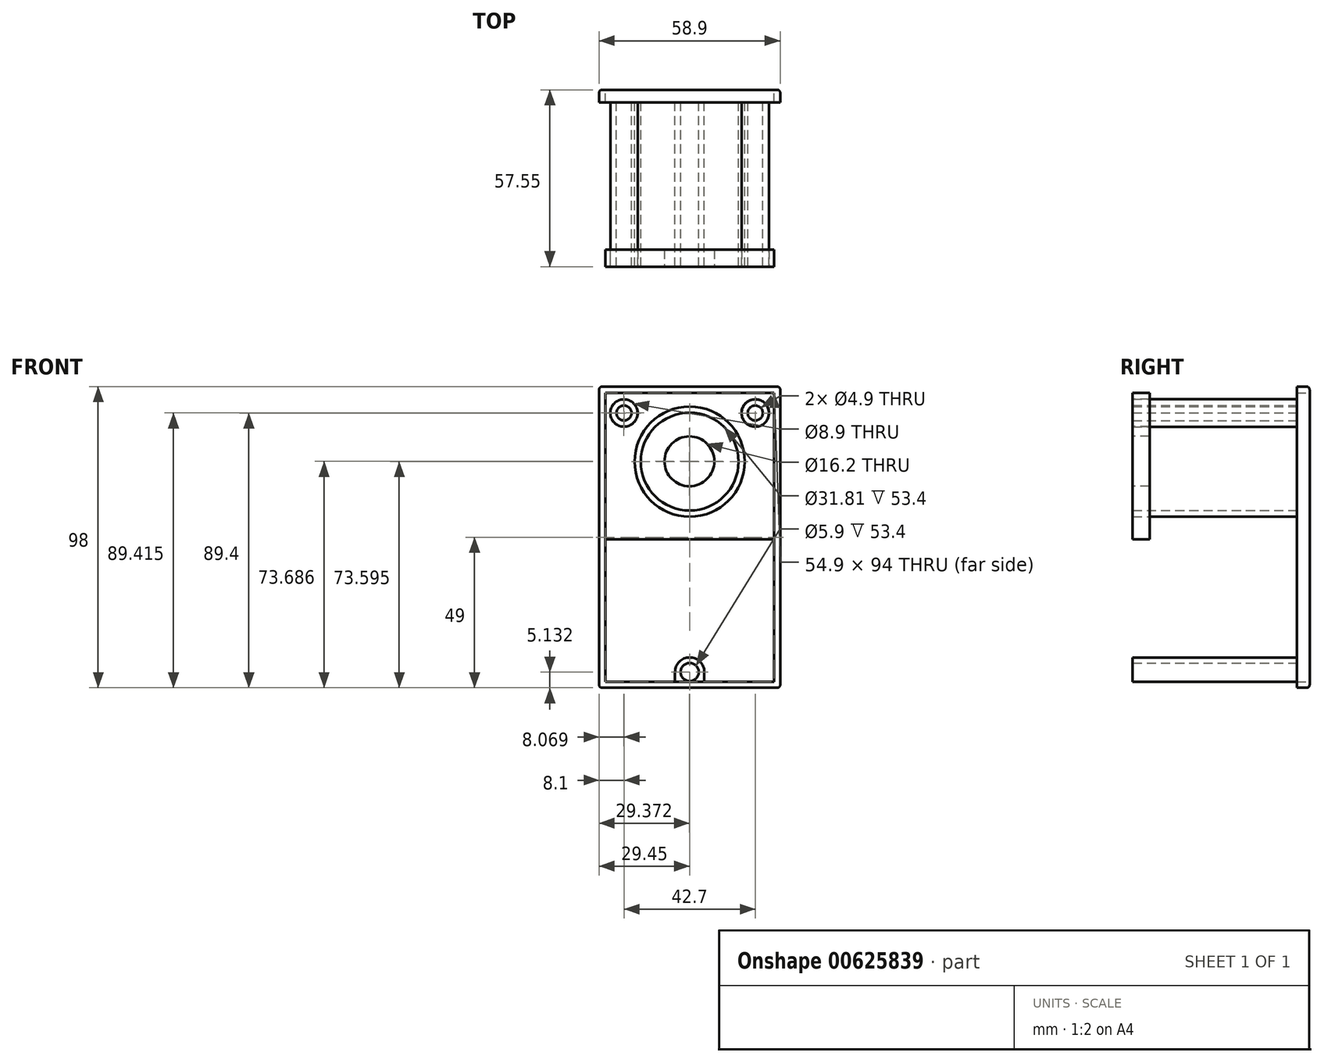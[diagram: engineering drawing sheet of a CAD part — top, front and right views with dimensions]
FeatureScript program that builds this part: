
annotation { "Feature Type Name" : "Feature", "Feature Type Description" : "" }
export const myFeature = defineFeature(function(context is Context, id is Id, definition is map)
    precondition{}
    {
        {
            var Q0;
            Q0=qCreatedBy(makeId("Front.planeOp"),FACE);
            var sketch = newSketch(context, id + "F0", { "sketchPlane" : qUnion([Q0])});
            skLineSegment(sketch, "E0.bottom", {"start": v(29.45, -49) * mm, "end": v(-29.45, -49) * mm});
            skLineSegment(sketch, "E0.top", {"start": v(29.45, 49) * mm, "end": v(-29.45, 49) * mm});
            skLineSegment(sketch, "E0.left", {"start": v(29.45, -49) * mm, "end": v(29.45, 49) * mm});
            skLineSegment(sketch, "E0.right", {"start": v(-29.45, -49) * mm, "end": v(-29.45, 49) * mm});
            skPoint(sketch, "E0.middle", {"position": v(0, 0) * mm});
            skCircle(sketch, "E1", {"center": v(0, 24.6) * mm, "radius": 15.9 * mm});
            skCircle(sketch, "E2", {"center": v(-21.35, 40.4) * mm, "radius": 4.4 * mm});
            skCircle(sketch, "E3", {"center": v(21.35, 40.4) * mm, "radius": 4.4 * mm});
            skCircle(sketch, "E4", {"center": v(-21.35, 40.4) * mm, "radius": 2.45 * mm});
            skCircle(sketch, "E5", {"center": v(21.35, 40.4) * mm, "radius": 2.45 * mm});
            skSolve(sketch);
        }
        {
            var Q0;
            Q0=makeQuery(id+"F0.imprint","IMPRINT",FACE,{"disambiguationData":[TD([[makeQuery(id+"F0.imprint","IMPRINT",EDGE,{"derivedFrom":sQuery(id+"F0.wireOp",EDGE,"E0.bottom")}),-1.0]])]});
            var Q1;
            Q1=makeQuery(id+"F0.imprint","IMPRINT",FACE,{"disambiguationData":[TD([[makeQuery(id+"F0.imprint","IMPRINT",EDGE,{"derivedFrom":sQuery(id+"F0.wireOp",EDGE,"E2")}),1.0]])]});
            var Q2;
            Q2=makeQuery(id+"F0.imprint","IMPRINT",FACE,{"disambiguationData":[TD([[makeQuery(id+"F0.imprint","IMPRINT",EDGE,{"derivedFrom":sQuery(id+"F0.wireOp",EDGE,"E3")}),1.0]])]});
            extrude(context, id + "F1", {"entities" : qUnion([Q0, Q1, Q2]), "depth" : 57.55 * mm, "offsetDistance" : 25 * mm});
        }
        {
            var Q0;
            Q0=makeQuery(id+"F1.opExtrude","CAP_FACE",FACE,{"disambiguationData":[OSD([sQuery(id+"F0.wireOp",EDGE,"E0.bottom"),sQuery(id+"F0.wireOp",EDGE,"E0.top"),sQuery(id+"F0.wireOp",EDGE,"E0.left"),sQuery(id+"F0.wireOp",EDGE,"E0.right"),sQuery(id+"F0.wireOp",EDGE,"E1"),sQuery(id+"F0.wireOp",EDGE,"E2"),sQuery(id+"F0.wireOp",EDGE,"E3")])],"isStart":false});
            shell(context, id + "F2", {"entities" : qUnion([Q0]), "thickness" : 2 * mm});
        }
        {
            var Q0;
            {var subQ0=sQuery(id+"F0.wireOp",EDGE,"E5");var subQ1=sQuery(id+"F0.wireOp",EDGE,"E4");var subQ2=sQuery(id+"F0.wireOp",EDGE,"E1");var subQ3=sQuery(id+"F0.wireOp",EDGE,"E0.right");var subQ4=sQuery(id+"F0.wireOp",EDGE,"E0.left");var subQ5=sQuery(id+"F0.wireOp",EDGE,"E0.top");var subQ6=sQuery(id+"F0.wireOp",EDGE,"E0.bottom");Q0=makeQuery(id+"F2.opShell","OFFSET_FACE",FACE,{"disambiguationData":[OSD([subQ6,subQ5,subQ4,subQ3,subQ2,subQ1,subQ0]),TDD([makeQuery(id+"F1.opExtrude","CAP_FACE",FACE,{"disambiguationData":[OSD([subQ6,subQ5,subQ4,subQ3,subQ2,subQ1,subQ0])],"isStart":false})]),OD(0.0)]});}
            extrude(context, id + "F3", {"entities" : qUnion([Q0]), "operationType" : NewBodyOperationType.REMOVE, "oppositeDirection" : true, "depth" : 53.4 * mm, "offsetDistance" : 25 * mm});
        }
        {
            var Q0;
            Q0=makeQuery(id+"F1.opExtrude","SWEPT_FACE",FACE,{"disambiguationData":[OSD([sQuery(id+"F0.wireOp",EDGE,"E0.left")])]});
            var sketch = newSketch(context, id + "F4", { "sketchPlane" : qUnion([Q0])});
            skLineSegment(sketch, "E6.bottom", {"start": v(-57.55, -0.66) * mm, "end": v(-38.05, -0.66) * mm});
            skLineSegment(sketch, "E6.top", {"start": v(-57.55, -39.66) * mm, "end": v(-38.05, -39.66) * mm});
            skLineSegment(sketch, "E6.left", {"start": v(-57.55, -0.66) * mm, "end": v(-57.55, -39.66) * mm});
            skLineSegment(sketch, "E6.right", {"start": v(-38.05, -0.66) * mm, "end": v(-38.05, -39.66) * mm});
            skSolve(sketch);
        }
        {
            var Q0;
            Q0=makeQuery(id+"F4.imprint","IMPRINT",FACE,{"disambiguationData":[TD([[makeQuery(id+"F4.imprint","IMPRINT",EDGE,{"derivedFrom":sQuery(id+"F4.wireOp",EDGE,"E6.bottom")}),-1.0]])]});
            extrude(context, id + "F5", {"entities" : qUnion([Q0]), "operationType" : NewBodyOperationType.REMOVE, "endBound" : BoundingType.THROUGH_ALL, "oppositeDirection" : true, "depth" : 25 * mm, "offsetDistance" : 25 * mm});
        }
        {
            var Q0;
            {var subQ0=sQuery(id+"F0.wireOp",EDGE,"E5");var subQ1=sQuery(id+"F0.wireOp",EDGE,"E4");var subQ2=sQuery(id+"F0.wireOp",EDGE,"E1");var subQ3=sQuery(id+"F0.wireOp",EDGE,"E0.right");var subQ4=sQuery(id+"F0.wireOp",EDGE,"E0.left");var subQ5=sQuery(id+"F0.wireOp",EDGE,"E0.top");var subQ6=sQuery(id+"F0.wireOp",EDGE,"E0.bottom");Q0=makeQuery(id+"F2.opShell","OFFSET_FACE",FACE,{"disambiguationData":[OSD([subQ6,subQ5,subQ4,subQ3,subQ2,subQ1,subQ0]),TDD([makeQuery(id+"F1.opExtrude","CAP_FACE",FACE,{"disambiguationData":[OSD([subQ6,subQ5,subQ4,subQ3,subQ2,subQ1,subQ0])],"isStart":true})])]});}
            var sketch = newSketch(context, id + "F6", { "sketchPlane" : qUnion([Q0])});
            skCircle(sketch, "E7", {"center": v(0, -43.87) * mm, "radius": 2.95 * mm});
            skPoint(sketch, "E7.centerSnap0", {"position": v(0, -46.53) * mm});
            skArc(sketch, "E8", {"start": v(-4.76, -43.87) * mm, "mid": v(0, -39.1) * mm, "end": v(4.76, -43.87) * mm});
            skLineSegment(sketch, "E9", {"start": v(-4.76, -43.87) * mm, "end": v(-4.76, -47) * mm});
            skLineSegment(sketch, "E10", {"start": v(4.76, -43.87) * mm, "end": v(4.76, -47) * mm});
            skSolve(sketch);
        }
        {
            var Q0;
            Q0=makeQuery(id+"F6.imprint","IMPRINT",FACE,{"disambiguationData":[TD([[makeQuery(id+"F6.imprint","IMPRINT",EDGE,{"derivedFrom":sQuery(id+"F6.wireOp",EDGE,"E7")}),-1.0]])]});
            extrude(context, id + "F7", {"entities" : qUnion([Q0]), "operationType" : NewBodyOperationType.ADD, "depth" : 55.55 * mm, "offsetDistance" : 25 * mm});
        }
        {
            var Q0;
            {var subQ0=sQuery(id+"F0.wireOp",EDGE,"E5");var subQ1=sQuery(id+"F0.wireOp",EDGE,"E4");var subQ2=sQuery(id+"F0.wireOp",EDGE,"E1");var subQ3=sQuery(id+"F0.wireOp",EDGE,"E0.right");var subQ4=sQuery(id+"F0.wireOp",EDGE,"E0.left");var subQ5=sQuery(id+"F0.wireOp",EDGE,"E0.top");var subQ6=sQuery(id+"F0.wireOp",EDGE,"E0.bottom");Q0=makeQuery(id+"F7.boolean.opBoolean","SPLIT",FACE,{"disambiguationData":[TD([makeQuery(id+"F7.opExtrude","SWEPT_FACE",FACE,{"disambiguationData":[OSD([sQuery(id+"F6.wireOp",EDGE,"E7")])]})])],"derivedFrom":makeQuery(id+"F2.opShell","OFFSET_FACE",FACE,{"disambiguationData":[OSD([subQ6,subQ5,subQ4,subQ3,subQ2,subQ1,subQ0]),TDD([makeQuery(id+"F1.opExtrude","CAP_FACE",FACE,{"disambiguationData":[OSD([subQ6,subQ5,subQ4,subQ3,subQ2,subQ1,subQ0])],"isStart":true})])]})});}
            extrude(context, id + "F8", {"entities" : qUnion([Q0]), "operationType" : NewBodyOperationType.REMOVE, "endBound" : BoundingType.THROUGH_ALL, "oppositeDirection" : true, "depth" : 25 * mm, "offsetDistance" : 25 * mm});
        }
        {
            var Q0;
            Q0=makeQuery(id+"F1.opExtrude","SWEPT_EDGE",EDGE,{"disambiguationData":[OSD([sQuery(id+"F0.wireOp",EDGE,"E0.top"),sQuery(id+"F0.wireOp",EDGE,"E0.left")])]});
            var Q1;
            Q1=makeQuery(id+"F1.opExtrude","SWEPT_EDGE",EDGE,{"disambiguationData":[OSD([sQuery(id+"F0.wireOp",EDGE,"E0.top"),sQuery(id+"F0.wireOp",EDGE,"E0.right")])]});
            var Q2;
            Q2=makeQuery(id+"F1.opExtrude","CAP_EDGE",EDGE,{"disambiguationData":[OSD([sQuery(id+"F0.wireOp",EDGE,"E0.top")])],"isStart":true});
            var Q3;
            Q3=makeQuery(id+"F1.opExtrude","CAP_EDGE",EDGE,{"disambiguationData":[OSD([sQuery(id+"F0.wireOp",EDGE,"E0.left")])],"isStart":true});
            var Q4;
            Q4=makeQuery(id+"F1.opExtrude","CAP_EDGE",EDGE,{"disambiguationData":[OSD([sQuery(id+"F0.wireOp",EDGE,"E0.right")])],"isStart":true});
            var Q5;
            Q5=makeQuery(id+"F1.opExtrude","SWEPT_EDGE",EDGE,{"disambiguationData":[OSD([sQuery(id+"F0.wireOp",EDGE,"E0.bottom"),sQuery(id+"F0.wireOp",EDGE,"E0.right")])]});
            var Q6;
            Q6=makeQuery(id+"F1.opExtrude","CAP_EDGE",EDGE,{"disambiguationData":[OSD([sQuery(id+"F0.wireOp",EDGE,"E0.bottom")])],"isStart":true});
            var Q7;
            Q7=makeQuery(id+"F1.opExtrude","SWEPT_EDGE",EDGE,{"disambiguationData":[OSD([sQuery(id+"F0.wireOp",EDGE,"E0.bottom"),sQuery(id+"F0.wireOp",EDGE,"E0.left")])]});
            fillet(context, id + "F9", {"entities" : qUnion([Q0, Q1, Q2, Q3, Q4, Q5, Q6, Q7]), "radius" : 1 * mm, "tangentPropagation" : true, "allowEdgeOverflow" : false});
        }
        {
            var Q0;
            Q0=makeQuery(id+"F3.boolean.opBoolean","COPY",FACE,{"derivedFrom":makeQuery(id+"F3.opExtrude","CAP_FACE",FACE,{"disambiguationData":[OSD([sQuery(id+"F0.wireOp",EDGE,"E0.bottom"),sQuery(id+"F0.wireOp",EDGE,"E0.top"),sQuery(id+"F0.wireOp",EDGE,"E0.left"),sQuery(id+"F0.wireOp",EDGE,"E0.right"),sQuery(id+"F0.wireOp",EDGE,"E1"),sQuery(id+"F0.wireOp",EDGE,"E4"),sQuery(id+"F0.wireOp",EDGE,"E5")])],"isStart":false})});
            var sketch = newSketch(context, id + "F10", { "sketchPlane" : qUnion([Q0])});
            skLineSegment(sketch, "E11.bottom", {"start": v(17.6, 21.28) * mm, "end": v(-17.6, 21.28) * mm});
            skLineSegment(sketch, "E11.top", {"start": v(17.6, 27.91) * mm, "end": v(-17.6, 27.91) * mm});
            skLineSegment(sketch, "E11.left", {"start": v(17.6, 21.28) * mm, "end": v(17.6, 27.91) * mm});
            skLineSegment(sketch, "E11.right", {"start": v(-17.6, 21.28) * mm, "end": v(-17.6, 27.91) * mm});
            skPoint(sketch, "E11.middle", {"position": v(0, 24.6) * mm});
            skSolve(sketch);
        }
        {
            var Q0;
            {var subQ0=sQuery(id+"F10.wireOp",EDGE,"E11.right");Q0=makeQuery(id+"F10.imprint","IMPRINT",FACE,{"disambiguationData":[TD([[makeQuery(id+"F10.imprint","IMPRINT",EDGE,{"derivedFrom":subQ0}),1.0]])]});}
            var Q1;
            {var subQ0=sQuery(id+"F10.wireOp",EDGE,"E11.right");Q1=makeQuery(id+"F10.imprint","IMPRINT",FACE,{"disambiguationData":[TD([[makeQuery(id+"F10.imprint","IMPRINT",EDGE,{"derivedFrom":subQ0}),-1.0]])]});}
            var Q2;
            {var subQ0=sQuery(id+"F10.wireOp",EDGE,"E11.left");Q2=makeQuery(id+"F10.imprint","IMPRINT",FACE,{"disambiguationData":[TD([[makeQuery(id+"F10.imprint","IMPRINT",EDGE,{"derivedFrom":subQ0}),1.0]])]});}
            var Q3;
            {var subQ0=sQuery(id+"F10.wireOp",EDGE,"E11.left");Q3=makeQuery(id+"F10.imprint","IMPRINT",FACE,{"disambiguationData":[TD([[makeQuery(id+"F10.imprint","IMPRINT",EDGE,{"derivedFrom":subQ0}),-1.0]])]});}
            extrude(context, id + "F11", {"entities" : qUnion([Q0, Q1, Q2, Q3]), "operationType" : NewBodyOperationType.REMOVE, "endBound" : BoundingType.THROUGH_ALL, "oppositeDirection" : true, "depth" : 25 * mm, "offsetDistance" : 25 * mm});
        }
        {
            var Q0;
            {var subQ0=sQuery(id+"F0.wireOp",EDGE,"E0.right");var subQ1=sQuery(id+"F0.wireOp",EDGE,"E0.left");var subQ2=sQuery(id+"F0.wireOp",EDGE,"E0.top");Q0=makeQuery(id+"F5.boolean.opBoolean","SPLIT",FACE,{"disambiguationData":[TD([makeQuery(id+"F1.opExtrude","SWEPT_FACE",FACE,{"disambiguationData":[OSD([subQ2])]})])],"derivedFrom":makeQuery(id+"F1.opExtrude","CAP_FACE",FACE,{"disambiguationData":[OSD([sQuery(id+"F0.wireOp",EDGE,"E0.bottom"),subQ2,subQ1,subQ0,sQuery(id+"F0.wireOp",EDGE,"E1"),sQuery(id+"F0.wireOp",EDGE,"E4"),sQuery(id+"F0.wireOp",EDGE,"E5")])],"isStart":false})});}
            var sketch = newSketch(context, id + "F12", { "sketchPlane" : qUnion([Q0])});
            skCircle(sketch, "E12", {"center": v(-21.38, 40.41) * mm, "radius": 4.45 * mm});
            skPoint(sketch, "E12.first.point", {"position": v(-24.38, 43.7) * mm});
            skPoint(sketch, "E12.second.point", {"position": v(-17.1, 41.6) * mm});
            skPoint(sketch, "E12.third.point", {"position": v(-22.48, 36.1) * mm});
            skCircle(sketch, "E13", {"center": v(21.34, 40.4) * mm, "radius": 4.46 * mm});
            skPoint(sketch, "E13.first.point", {"position": v(17.51, 42.7) * mm});
            skPoint(sketch, "E13.second.point", {"position": v(25.18, 42.68) * mm});
            skPoint(sketch, "E13.third.point", {"position": v(21.36, 35.94) * mm});
            skLineSegment(sketch, "E14.bottom", {"start": v(-27.45, 47) * mm, "end": v(27.45, 47) * mm});
            skLineSegment(sketch, "E14.top", {"start": v(-27.45, -0.66) * mm, "end": v(27.45, -0.66) * mm});
            skLineSegment(sketch, "E14.left", {"start": v(-27.45, 47) * mm, "end": v(-27.45, -0.66) * mm});
            skLineSegment(sketch, "E14.right", {"start": v(27.45, 47) * mm, "end": v(27.45, -0.66) * mm});
            skCircle(sketch, "E15", {"center": v(-0.08, 24.69) * mm, "radius": 8.1 * mm});
            skSolve(sketch);
        }
        {
            var Q0;
            Q0=makeQuery(id+"F12.imprint","IMPRINT",FACE,{"disambiguationData":[TD([[makeQuery(id+"F12.imprint","IMPRINT",EDGE,{"derivedFrom":sQuery(id+"F12.wireOp",EDGE,"E12")}),-1.0]])]});
            extrude(context, id + "F13", {"entities" : qUnion([Q0]), "oppositeDirection" : true, "depth" : 5.5 * mm, "offsetDistance" : 25 * mm});
        }
    });
